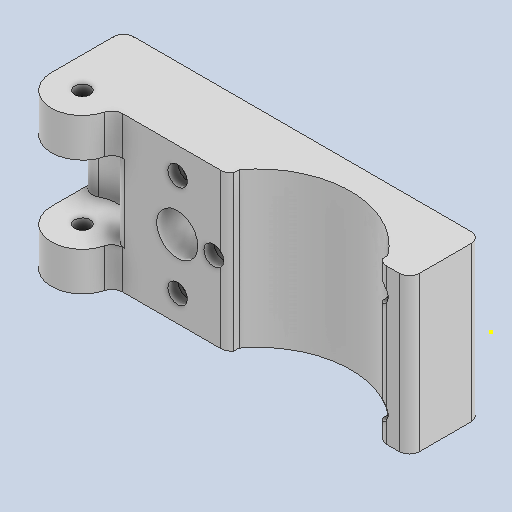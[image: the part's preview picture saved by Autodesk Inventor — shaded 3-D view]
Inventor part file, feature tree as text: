
AUTODESK INVENTOR PART (.ipt)
format: ipt  version: 2023.1 (Build 271208000, 208)  size: 395,776 bytes
history: native  units: mm
features: extrude x10, sketch x7, fillet x1
ambient origin geometry x8: Origin, YZ Plane, XZ Plane, XY Plane, X Axis, Y Axis, Z Axis, Center Point
bodies: Solid1 (feature_tree)
feature tree (18):
  sketch  "Sketch2"  dims[d3=2.0mm d12=3.5mm]
  extrude  "Extrusion1"  Depth=2.0mm
  extrude  "Extrusion2"  Depth=8.5mm
  extrude  "Extrusion10"  Depth=2.0mm
  fillet  "Fillet4"  Radius=2.0mm
  extrude  "Extrusion15"  TaperAngle=0.0deg  [1 undecoded]
  extrude  "Extrusion16"  Depth=15.0mm TaperAngle=0.0deg
  sketch  "Sketch32"  dims[d21=0.0mm d22=0.0mm]
  sketch  "Sketch33"  dims[d26=30.0mm d27=0.0mm d28=15.0mm d29=0.0mm]
  extrude  "Extrusion36"  Depth=1.0mm
  sketch  "Sketch42"  dims[d62=10.0mm d63=0.0mm d91=3.932363mm d92=2.0mm d93=28.0mm d94=2.0mm d95=2.0mm d99=8.0mm d101=15.0mm d102=0.0mm d103=11.0mm d104=6.0mm d105=0.0mm d106=47.0mm d107=10.0mm d254=2.2mm d255=19.8mm d256=39.0mm d257=5.1mm d258=6.0mm d259=9.9mm d260=30.5mm d261=1.5mm d262=20.0mm d263=0.0mm d264=3.8mm d265=2.0mm d266=0.0mm d267=7.25mm d268=0.0mm d269=7.25mm d270=0.0mm d271=7.25mm d272=0.0mm d45=0.0mm d46=0.0mm d47=0.0mm d48=0.0mm d52=0.0mm d53=0.0mm d54=0.0mm d55=0.0mm d67=0.5mm d68=0.872665mm d69=0.5mm d70=0.872665mm d180=0.5mm d181=0.872665mm d182=0.5mm d183=0.872665mm]
  extrude  "Extrusion37"  Depth=7.25mm
  extrude  "Extrusion38"  Depth=2.0mm
  extrude  "Extrusion39"  Depth=7.25mm
  extrude  "Extrusion40"  Depth=2.0mm
  sketch  "Sketch13"  dims[d13=30.0mm d14=8.5mm]
  sketch  "Sketch14"  dims[d17=3.0mm d18=2.0mm d19=2.0mm]
  sketch  "Sketch41"  dims[d59=1.0mm d60=1.0mm]
note: 1 required parameter value undecoded (feature->parameter linkage not recoverable at this tier; creation-order binding heuristic only, values carry confidence <= 0.55)
